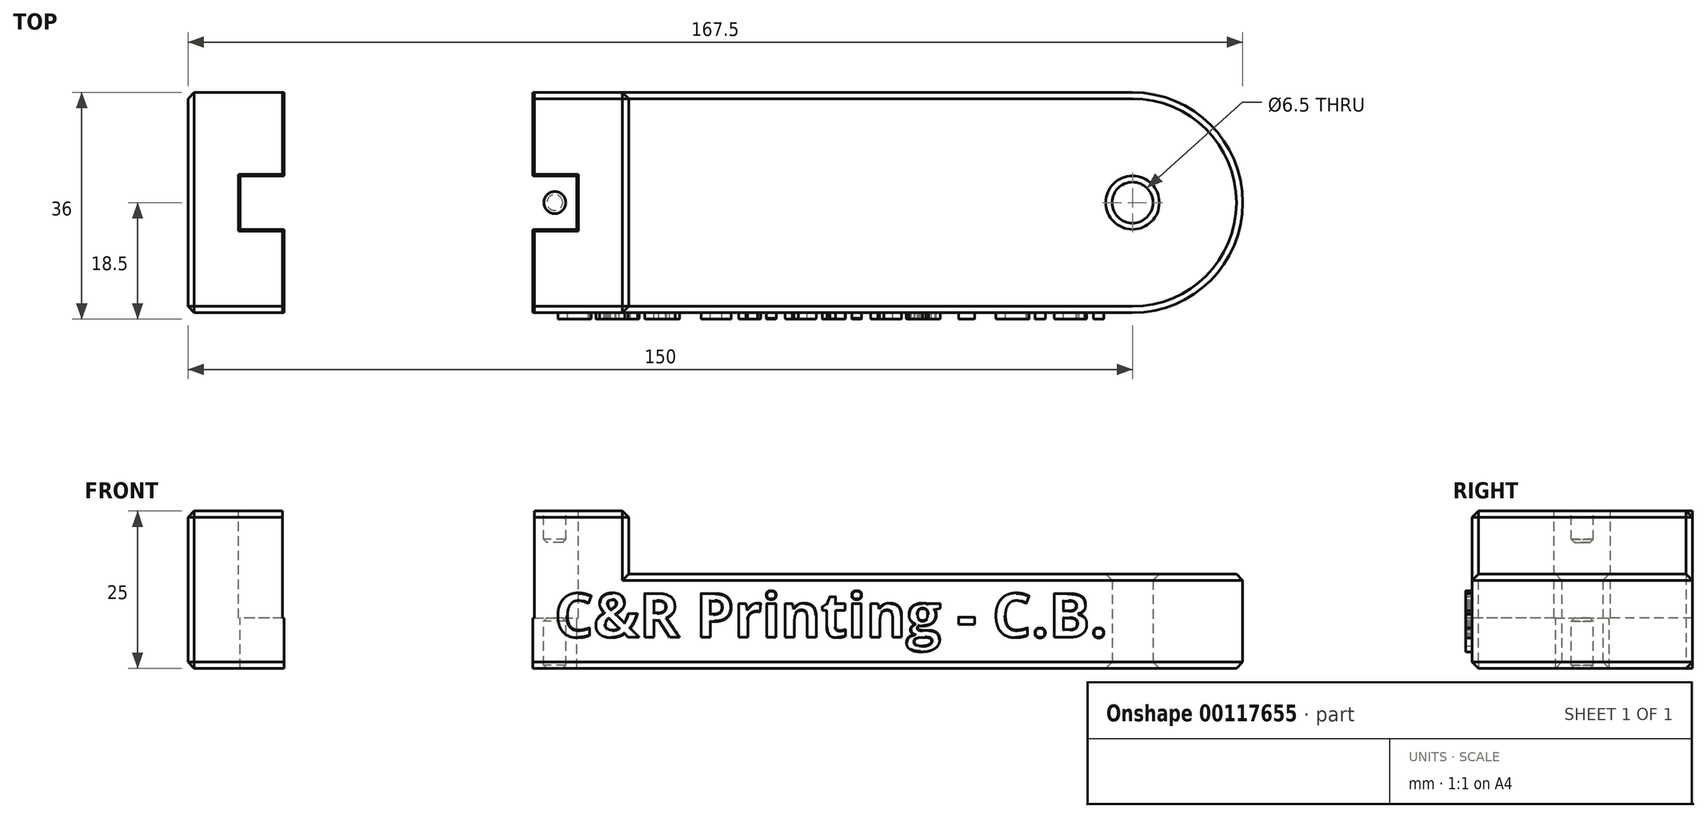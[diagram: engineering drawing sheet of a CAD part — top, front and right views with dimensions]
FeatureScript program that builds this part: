
annotation { "Feature Type Name" : "Feature", "Feature Type Description" : "" }
export const myFeature = defineFeature(function(context is Context, id is Id, definition is map)
    precondition{}
    {
        {
            var Q0;
            Q0=qCreatedBy(makeId("Top.planeOp"),FACE);
            var sketch = newSketch(context, id + "F0", { "sketchPlane" : qUnion([Q0])});
            skLineSegment(sketch, "E0.bottom", {"start": v(75, -17.5) * mm, "end": v(-75, -17.5) * mm});
            skLineSegment(sketch, "E0.top", {"start": v(75, 17.5) * mm, "end": v(-75, 17.5) * mm});
            skLineSegment(sketch, "E0.right", {"start": v(-75, -17.5) * mm, "end": v(-75, 17.5) * mm});
            skPoint(sketch, "E0.middle", {"position": v(0, 0) * mm});
            skPoint(sketch, "E1", {"position": v(75, 0) * mm});
            skArc(sketch, "E2", {"start": v(75, -17.5) * mm, "mid": v(92.5, 0) * mm, "end": v(75, 17.5) * mm});
            skCircle(sketch, "E3", {"center": v(75, 0) * mm, "radius": 3.25 * mm});
            skSolve(sketch);
        }
        {
            var Q0;
            Q0 = qSketchRegion(id + "F0", true);
            extrude(context, id + "F1", {"entities" : qUnion([Q0]), "depth" : 15 * mm});
        }
        {
            var Q0;
            Q0=makeQuery(id+"F1.opExtrude","CAP_FACE",FACE,{"disambiguationData":[OSD([sQuery(id+"F0.wireOp",EDGE,"E0.bottom"),sQuery(id+"F0.wireOp",EDGE,"E0.top"),sQuery(id+"F0.wireOp",EDGE,"E0.right"),sQuery(id+"F0.wireOp",EDGE,"E2"),sQuery(id+"F0.wireOp",EDGE,"E3")])],"isStart":false});
            var sketch = newSketch(context, id + "F2", { "sketchPlane" : qUnion([Q0])});
            skLineSegment(sketch, "E4.bottom", {"start": v(-75, 17.5) * mm, "end": v(-5, 17.5) * mm});
            skLineSegment(sketch, "E4.top", {"start": v(-75, -17.5) * mm, "end": v(-5, -17.5) * mm});
            skLineSegment(sketch, "E4.left", {"start": v(-75, 17.5) * mm, "end": v(-75, -17.5) * mm});
            skLineSegment(sketch, "E4.right", {"start": v(-5, 17.5) * mm, "end": v(-5, -17.5) * mm});
            skPoint(sketch, "E5", {"position": v(-60, 17.5) * mm});
            skLineSegment(sketch, "E6.bottom", {"start": v(-60, 17.5) * mm, "end": v(-20, 17.5) * mm});
            skLineSegment(sketch, "E6.top", {"start": v(-60, -17.5) * mm, "end": v(-20, -17.5) * mm});
            skLineSegment(sketch, "E6.right", {"start": v(-20, 17.5) * mm, "end": v(-20, -17.5) * mm});
            skLineSegment(sketch, "E7.bottom", {"start": v(-60, -4.5) * mm, "end": v(-67, -4.5) * mm});
            skLineSegment(sketch, "E7.top", {"start": v(-60, 4.5) * mm, "end": v(-67, 4.5) * mm});
            skLineSegment(sketch, "E7.right", {"start": v(-67, -4.5) * mm, "end": v(-67, 4.5) * mm});
            skPoint(sketch, "E8", {"position": v(-40, 17.5) * mm});
            skLineSegment(sketch, "E9", {"start": v(-40, 82.16) * mm, "end": v(-40, 3333.7) * mm, "construction": true});
            skLineSegment(sketch, "E10", {"start": v(-67, 4.5) * mm, "end": v(-67, 17.5) * mm});
            skLineSegment(sketch, "E11", {"start": v(-60, 17.5) * mm, "end": v(-67, 17.5) * mm});
            skLineSegment(sketch, "E12", {"start": v(-67, -4.5) * mm, "end": v(-67, -17.5) * mm});
            skLineSegment(sketch, "E13", {"start": v(-60, -17.5) * mm, "end": v(-67, -17.5) * mm});
            skLineSegment(sketch, "E14.MirrorCS", {"start": v(-13, 4.5) * mm, "end": v(-13, 17.5) * mm});
            skLineSegment(sketch, "E15.MirrorCS", {"start": v(-20, 4.5) * mm, "end": v(-13, 4.5) * mm});
            skLineSegment(sketch, "E16.MirrorCS", {"start": v(-20, -4.5) * mm, "end": v(-13, -4.5) * mm});
            skLineSegment(sketch, "E17.MirrorCS", {"start": v(-13, -4.5) * mm, "end": v(-13, 4.5) * mm});
            skLineSegment(sketch, "E18.MirrorCS", {"start": v(-13, -4.5) * mm, "end": v(-13, -17.5) * mm});
            skLineSegment(sketch, "E19.MirrorCS", {"start": v(-20, -17.5) * mm, "end": v(-13, -17.5) * mm});
            skLineSegment(sketch, "E20", {"start": v(-20, 17.5) * mm, "end": v(-13, 17.5) * mm});
            skLineSegment(sketch, "E21", {"start": v(-60, 17.5) * mm, "end": v(-60, -17.5) * mm});
            skPoint(sketch, "E22", {"position": v(-5, 0) * mm});
            skPoint(sketch, "E23", {"position": v(-40, -17.5) * mm});
            skPoint(sketch, "E24", {"position": v(-75, 0) * mm});
            skPoint(sketch, "E25", {"position": v(-40, 0) * mm});
            skSolve(sketch);
        }
        {
            var Q0;
            Q0 = qSketchRegion(id + "F2", true);
            var Q1;
            {var subQ0=sQuery(id+"F2.wireOp",EDGE,"E7.top");Q1=makeQuery(id+"F2.imprint","IMPRINT",FACE,{"disambiguationData":[TD([[makeQuery(id+"F2.imprint","IMPRINT",EDGE,{"derivedFrom":subQ0}),-1.0]])]});}
            var Q2;
            {var subQ0=sQuery(id+"F2.wireOp",EDGE,"E7.bottom");Q2=makeQuery(id+"F2.imprint","IMPRINT",FACE,{"disambiguationData":[TD([[makeQuery(id+"F2.imprint","IMPRINT",EDGE,{"derivedFrom":subQ0}),-1.0]])]});}
            var Q3;
            {var subQ0=sQuery(id+"F2.wireOp",EDGE,"E7.bottom");Q3=makeQuery(id+"F2.imprint","IMPRINT",FACE,{"disambiguationData":[TD([[makeQuery(id+"F2.imprint","IMPRINT",EDGE,{"derivedFrom":subQ0}),1.0]])]});}
            var Q4;
            {var subQ4=sQuery(id+"F2.wireOp",EDGE,"E6.bottom");Q4=makeQuery(id+"F2.imprint","IMPRINT",FACE,{"disambiguationData":[TD([[makeQuery(id+"F2.imprint","IMPRINT",EDGE,{"derivedFrom":subQ4}),-1.0]])]});}
            var Q5;
            {var subQ2=sQuery(id+"F2.wireOp",EDGE,"E16.MirrorCS");Q5=makeQuery(id+"F2.imprint","IMPRINT",FACE,{"disambiguationData":[TD([[makeQuery(id+"F2.imprint","IMPRINT",EDGE,{"derivedFrom":subQ2}),-1.0]])]});}
            var Q6;
            {var subQ0=sQuery(id+"F2.wireOp",EDGE,"E15.MirrorCS");Q6=makeQuery(id+"F2.imprint","IMPRINT",FACE,{"disambiguationData":[TD([[makeQuery(id+"F2.imprint","IMPRINT",EDGE,{"derivedFrom":subQ0}),-1.0]])]});}
            var Q7;
            Q7=makeQuery(id+"F2.imprint","IMPRINT",FACE,{"disambiguationData":[TD([[makeQuery(id+"F2.imprint","IMPRINT",EDGE,{"derivedFrom":sQuery(id+"F2.wireOp",EDGE,"E14.MirrorCS")}),1.0]])]});
            extrude(context, id + "F3", {"entities" : qUnion([Q0, Q1, Q2, Q3, Q4, Q5, Q6, Q7]), "operationType" : NewBodyOperationType.ADD, "depth" : 10 * mm});
        }
        {
            var Q0;
            Q0=makeQuery(id+"F3.opExtrude","CAP_FACE",FACE,{"disambiguationData":[OSD([sQuery(id+"F2.wireOp",EDGE,"E4.bottom"),sQuery(id+"F2.wireOp",EDGE,"E4.top"),sQuery(id+"F2.wireOp",EDGE,"E4.left"),sQuery(id+"F2.wireOp",EDGE,"E4.right")])],"isStart":false});
            cPlane(context, id + "F4", {"entities" : qUnion([Q0]), "cplaneType" : CPlaneType.OFFSET, "offset" : 0 * mm, "width" : 150 * mm, "height" : 150 * mm});
        }
        {
            var Q0;
            Q0=qCreatedBy(id+"F4.planeOp",FACE);
            var sketch = newSketch(context, id + "F5", { "sketchPlane" : qUnion([Q0])});
            skLineSegment(sketch, "E26.0", {"start": v(-20, 17.5) * mm, "end": v(-20, -17.5) * mm});
            skLineSegment(sketch, "E26.1", {"start": v(-60, 4.5) * mm, "end": v(-67, 4.5) * mm});
            skLineSegment(sketch, "E26.2", {"start": v(-67, -4.5) * mm, "end": v(-67, 4.5) * mm});
            skLineSegment(sketch, "E26.3", {"start": v(-13, -4.5) * mm, "end": v(-13, 4.5) * mm});
            skLineSegment(sketch, "E26.4", {"start": v(-67, 4.5) * mm, "end": v(-67, 17.5) * mm});
            skLineSegment(sketch, "E26.5", {"start": v(-60, 17.5) * mm, "end": v(-60, -17.5) * mm});
            skLineSegment(sketch, "E26.6", {"start": v(-13, 4.5) * mm, "end": v(-13, 17.5) * mm});
            skLineSegment(sketch, "E26.7", {"start": v(-60, -17.5) * mm, "end": v(-67, -17.5) * mm});
            skLineSegment(sketch, "E26.8", {"start": v(-60, -4.5) * mm, "end": v(-67, -4.5) * mm});
            skLineSegment(sketch, "E26.9", {"start": v(-20, -4.5) * mm, "end": v(-13, -4.5) * mm});
            skLineSegment(sketch, "E26.10", {"start": v(-20, 4.5) * mm, "end": v(-13, 4.5) * mm});
            skLineSegment(sketch, "E26.11", {"start": v(-20, -17.5) * mm, "end": v(-13, -17.5) * mm});
            skLineSegment(sketch, "E26.12", {"start": v(-60, 17.5) * mm, "end": v(-67, 17.5) * mm});
            skLineSegment(sketch, "E26.13", {"start": v(-67, -4.5) * mm, "end": v(-67, -17.5) * mm});
            skLineSegment(sketch, "E26.14", {"start": v(-60, -17.5) * mm, "end": v(-20, -17.5) * mm});
            skLineSegment(sketch, "E26.15", {"start": v(-60, 17.5) * mm, "end": v(-20, 17.5) * mm});
            skLineSegment(sketch, "E26.16", {"start": v(-20, 17.5) * mm, "end": v(-13, 17.5) * mm});
            skLineSegment(sketch, "E26.17", {"start": v(-13, -4.5) * mm, "end": v(-13, -17.5) * mm});
            skSolve(sketch);
        }
        {
            var Q0;
            {var subQ0=sQuery(id+"F5.wireOp",EDGE,"E26.1");Q0=makeQuery(id+"F5.imprint","IMPRINT",FACE,{"disambiguationData":[TD([[makeQuery(id+"F5.imprint","IMPRINT",EDGE,{"derivedFrom":subQ0}),1.0]])]});}
            var Q1;
            {var subQ6=sQuery(id+"F5.wireOp",EDGE,"E26.14");Q1=makeQuery(id+"F5.imprint","IMPRINT",FACE,{"disambiguationData":[TD([[makeQuery(id+"F5.imprint","IMPRINT",EDGE,{"derivedFrom":subQ6}),1.0]])]});}
            var Q2;
            Q2=makeQuery(id+"F5.imprint","IMPRINT",FACE,{"disambiguationData":[TD([[makeQuery(id+"F5.imprint","IMPRINT",EDGE,{"derivedFrom":sQuery(id+"F5.wireOp",EDGE,"E26.3")}),1.0]])]});
            extrude(context, id + "F6", {"entities" : qUnion([Q0, Q1, Q2]), "operationType" : NewBodyOperationType.REMOVE, "oppositeDirection" : true, "depth" : 17 * mm});
        }
        {
            var Q0;
            Q0 = qSketchRegion(id + "F5", true);
            extrude(context, id + "F7", {"entities" : qUnion([Q0]), "oppositeDirection" : true, "depth" : 5 * mm});
        }
        {
            var Q0;
            Q0=makeQuery(id+"F1.opExtrude","SWEPT_BODY",BODY,{"disambiguationData":[OSD([sQuery(id+"F0.wireOp",EDGE,"E0.bottom"),sQuery(id+"F0.wireOp",EDGE,"E0.top"),sQuery(id+"F0.wireOp",EDGE,"E0.right"),sQuery(id+"F0.wireOp",EDGE,"E2"),sQuery(id+"F0.wireOp",EDGE,"E3")])]});
            var Q1;
            Q1=makeQuery(id+"F7.opExtrude","SWEPT_BODY",BODY,{"disambiguationData":[OSD([sQuery(id+"F5.wireOp",EDGE,"E26.2"),sQuery(id+"F5.wireOp",EDGE,"E26.3"),sQuery(id+"F5.wireOp",EDGE,"E26.4"),sQuery(id+"F5.wireOp",EDGE,"E26.6"),sQuery(id+"F5.wireOp",EDGE,"E26.7"),sQuery(id+"F5.wireOp",EDGE,"E26.11"),sQuery(id+"F5.wireOp",EDGE,"E26.12"),sQuery(id+"F5.wireOp",EDGE,"E26.13"),sQuery(id+"F5.wireOp",EDGE,"E26.14"),sQuery(id+"F5.wireOp",EDGE,"E26.15"),sQuery(id+"F5.wireOp",EDGE,"E26.16"),sQuery(id+"F5.wireOp",EDGE,"E26.17")])]});
            var Q2;
            Q2=makeQuery(id+"F6.boolean.opBoolean","COPY",FACE,{"derivedFrom":makeQuery(id+"F6.opExtrude","SWEPT_FACE",FACE,{"disambiguationData":[OSD([sQuery(id+"F5.wireOp",EDGE,"E26.1")])]})});
            var Q3;
            Q3=makeQuery(id+"F6.boolean.opBoolean","COPY",FACE,{"derivedFrom":makeQuery(id+"F6.opExtrude","SWEPT_FACE",FACE,{"disambiguationData":[OSD([sQuery(id+"F5.wireOp",EDGE,"E26.2")])]})});
            var Q4;
            Q4=makeQuery(id+"F6.boolean.opBoolean","COPY",FACE,{"derivedFrom":makeQuery(id+"F6.opExtrude","SWEPT_FACE",FACE,{"disambiguationData":[OSD([sQuery(id+"F5.wireOp",EDGE,"E26.8")])]})});
            var Q5;
            {var subQ0=sQuery(id+"F5.wireOp",EDGE,"E26.5");Q5=makeQuery(id+"F6.boolean.opBoolean","COPY",FACE,{"derivedFrom":makeQuery(id+"F6.opExtrude","SWEPT_FACE",FACE,{"disambiguationData":[OSD([subQ0]),TDD([makeQuery(id+"F5.imprint","IMPRINT",EDGE,{"disambiguationData":[TD([[makeQuery(id+"F5.imprint","INTERSECT",VERTEX,{"derivedFrom":[subQ0,sQuery(id+"F5.wireOp",EDGE,"E26.8")]}),-1.0]])],"derivedFrom":subQ0})])]})});}
            var Q6;
            {var subQ0=sQuery(id+"F5.wireOp",EDGE,"E26.5");Q6=makeQuery(id+"F6.boolean.opBoolean","COPY",FACE,{"derivedFrom":makeQuery(id+"F6.opExtrude","SWEPT_FACE",FACE,{"disambiguationData":[OSD([subQ0]),TDD([makeQuery(id+"F5.imprint","IMPRINT",EDGE,{"disambiguationData":[TD([[makeQuery(id+"F5.imprint","INTERSECT",VERTEX,{"derivedFrom":[sQuery(id+"F5.wireOp",EDGE,"E26.1"),subQ0]}),1.0]])],"derivedFrom":subQ0})])]})});}
            var Q7;
            {var subQ0=sQuery(id+"F5.wireOp",EDGE,"E26.0");Q7=makeQuery(id+"F6.boolean.opBoolean","COPY",FACE,{"derivedFrom":makeQuery(id+"F6.opExtrude","SWEPT_FACE",FACE,{"disambiguationData":[OSD([subQ0]),TDD([makeQuery(id+"F5.imprint","IMPRINT",EDGE,{"disambiguationData":[TD([[makeQuery(id+"F5.imprint","INTERSECT",VERTEX,{"derivedFrom":[subQ0,sQuery(id+"F5.wireOp",EDGE,"E26.9")]}),-1.0]])],"derivedFrom":subQ0})])]})});}
            var Q8;
            Q8=makeQuery(id+"F6.boolean.opBoolean","COPY",FACE,{"derivedFrom":makeQuery(id+"F6.opExtrude","SWEPT_FACE",FACE,{"disambiguationData":[OSD([sQuery(id+"F5.wireOp",EDGE,"E26.3")])]})});
            var Q9;
            {var subQ0=sQuery(id+"F5.wireOp",EDGE,"E26.0");Q9=makeQuery(id+"F6.boolean.opBoolean","COPY",FACE,{"derivedFrom":makeQuery(id+"F6.opExtrude","SWEPT_FACE",FACE,{"disambiguationData":[OSD([subQ0]),TDD([makeQuery(id+"F5.imprint","IMPRINT",EDGE,{"disambiguationData":[TD([[makeQuery(id+"F5.imprint","INTERSECT",VERTEX,{"derivedFrom":[subQ0,sQuery(id+"F5.wireOp",EDGE,"E26.10")]}),1.0]])],"derivedFrom":subQ0})])]})});}
            var Q10;
            Q10=makeQuery(id+"F6.boolean.opBoolean","COPY",FACE,{"derivedFrom":makeQuery(id+"F6.opExtrude","SWEPT_FACE",FACE,{"disambiguationData":[OSD([sQuery(id+"F5.wireOp",EDGE,"E26.10")])]})});
            var Q11;
            Q11=makeQuery(id+"F6.boolean.opBoolean","COPY",FACE,{"derivedFrom":makeQuery(id+"F6.opExtrude","SWEPT_FACE",FACE,{"disambiguationData":[OSD([sQuery(id+"F5.wireOp",EDGE,"E26.9")])]})});
            booleanBodies(context, id + "F8", {"operationType" : BooleanOperationType.SUBTRACTION, "tools" : qUnion([Q0]), "targets" : qUnion([Q1]), "offset" : true, "entitiesToOffset" : qUnion([Q2, Q3, Q4, Q5, Q6, Q7, Q8, Q9, Q10, Q11]), "offsetDistance" : .25 * mm, "keepTools" : true});
        }
        {
            var Q0;
            Q0=makeQuery(id+"F7.opExtrude","CAP_FACE",FACE,{"disambiguationData":[OSD([sQuery(id+"F5.wireOp",EDGE,"E26.2"),sQuery(id+"F5.wireOp",EDGE,"E26.3"),sQuery(id+"F5.wireOp",EDGE,"E26.4"),sQuery(id+"F5.wireOp",EDGE,"E26.6"),sQuery(id+"F5.wireOp",EDGE,"E26.7"),sQuery(id+"F5.wireOp",EDGE,"E26.11"),sQuery(id+"F5.wireOp",EDGE,"E26.12"),sQuery(id+"F5.wireOp",EDGE,"E26.13"),sQuery(id+"F5.wireOp",EDGE,"E26.14"),sQuery(id+"F5.wireOp",EDGE,"E26.15"),sQuery(id+"F5.wireOp",EDGE,"E26.16"),sQuery(id+"F5.wireOp",EDGE,"E26.17")])],"isStart":true});
            var sketch = newSketch(context, id + "F9", { "sketchPlane" : qUnion([Q0])});
            skPoint(sketch, "E27", {"position": v(-66.75, 4.25) * mm});
            skPoint(sketch, "E28", {"position": v(-59.75, 4.25) * mm});
            skPoint(sketch, "E29", {"position": v(-63.25, 4.25) * mm});
            skPoint(sketch, "E30", {"position": v(-66.75, 0) * mm});
            skPoint(sketch, "E31", {"position": v(-63.25, 0) * mm});
            skLineSegment(sketch, "E32", {"start": v(-40, 25.57) * mm, "end": v(-40, -23.42) * mm, "construction": true});
            skPoint(sketch, "E32.startSnap0", {"position": v(-40, 17.5) * mm});
            skPoint(sketch, "E33.MirrorP", {"position": v(-16.75, 0) * mm});
            skCircle(sketch, "E34", {"center": v(-63.25, 0) * mm, "radius": 1.75 * mm});
            skCircle(sketch, "E35.MirrorC", {"center": v(-16.75, 0) * mm, "radius": 1.75 * mm});
            skSolve(sketch);
        }
        {
            var Q0;
            Q0=makeQuery(id+"F9.imprint","IMPRINT",FACE,{"disambiguationData":[TD([[makeQuery(id+"F9.imprint","IMPRINT",EDGE,{"derivedFrom":sQuery(id+"F9.wireOp",EDGE,"E34")}),1.0]])]});
            var Q1;
            Q1=makeQuery(id+"F9.imprint","IMPRINT",FACE,{"disambiguationData":[TD([[makeQuery(id+"F9.imprint","IMPRINT",EDGE,{"derivedFrom":sQuery(id+"F9.wireOp",EDGE,"E35.MirrorC")}),-1.0]])]});
            extrude(context, id + "F10", {"entities" : qUnion([Q0, Q1]), "operationType" : NewBodyOperationType.REMOVE, "endBound" : BoundingType.THROUGH_ALL, "oppositeDirection" : true, "depth" : 25 * mm});
        }
        {
            var Q0;
            Q0=makeQuery(id+"F1.opExtrude","CAP_EDGE",EDGE,{"disambiguationData":[OSD([sQuery(id+"F0.wireOp",EDGE,"E3")])],"isStart":true});
            var Q1;
            Q1=makeQuery(id+"F1.opExtrude","CAP_EDGE",EDGE,{"disambiguationData":[OSD([sQuery(id+"F0.wireOp",EDGE,"E3")])],"isStart":false});
            var Q2;
            Q2=makeQuery(id+"F1.opExtrude","CAP_EDGE",EDGE,{"disambiguationData":[OSD([sQuery(id+"F0.wireOp",EDGE,"E0.bottom")])],"isStart":false});
            var Q3;
            Q3=makeQuery(id+"F1.opExtrude","CAP_EDGE",EDGE,{"disambiguationData":[OSD([sQuery(id+"F0.wireOp",EDGE,"E0.bottom")])],"isStart":true});
            var Q4;
            Q4=makeQuery(id+"F1.opExtrude","CAP_EDGE",EDGE,{"disambiguationData":[OSD([sQuery(id+"F0.wireOp",EDGE,"E0.right")])],"isStart":true});
            var Q5;
            Q5=makeQuery(id+"F3.opExtrude","CAP_EDGE",EDGE,{"disambiguationData":[OSD([sQuery(id+"F2.wireOp",EDGE,"E4.left")])],"isStart":false});
            var Q6;
            {var subQ0=sQuery(id+"F2.wireOp",EDGE,"E19.MirrorCS");var subQ1=sQuery(id+"F2.wireOp",EDGE,"E13");var subQ2=sQuery(id+"F2.wireOp",EDGE,"E6.top");var subQ4=sQuery(id+"F2.wireOp",EDGE,"E4.top");Q6=makeQuery(id+"F6.boolean.opBoolean","SPLIT",EDGE,{"disambiguationData":[TD([makeQuery(id+"F1.opExtrude","SWEPT_FACE",FACE,{"disambiguationData":[OSD([sQuery(id+"F0.wireOp",EDGE,"E0.right")])]})])],"derivedFrom":makeQuery(id+"F3.opExtrude","CAP_EDGE",EDGE,{"disambiguationData":[OSD([subQ4,subQ2,subQ1,subQ0])],"isStart":false})});}
            var Q7;
            {var subQ0=sQuery(id+"F2.wireOp",EDGE,"E4.right");var subQ1=sQuery(id+"F2.wireOp",EDGE,"E19.MirrorCS");var subQ2=sQuery(id+"F2.wireOp",EDGE,"E13");var subQ3=sQuery(id+"F2.wireOp",EDGE,"E6.top");var subQ4=sQuery(id+"F2.wireOp",EDGE,"E4.top");Q7=makeQuery(id+"F6.boolean.opBoolean","SPLIT",EDGE,{"disambiguationData":[TD([makeQuery(id+"F3.opExtrude","SWEPT_FACE",FACE,{"disambiguationData":[OSD([subQ0])]})])],"derivedFrom":makeQuery(id+"F3.opExtrude","CAP_EDGE",EDGE,{"disambiguationData":[OSD([subQ4,subQ3,subQ2,subQ1])],"isStart":false})});}
            var Q8;
            Q8=makeQuery(id+"F3.opExtrude","CAP_EDGE",EDGE,{"disambiguationData":[OSD([sQuery(id+"F2.wireOp",EDGE,"E4.right")])],"isStart":false});
            var Q9;
            {var subQ0=sQuery(id+"F2.wireOp",EDGE,"E4.right");var subQ1=sQuery(id+"F2.wireOp",EDGE,"E20");var subQ2=sQuery(id+"F2.wireOp",EDGE,"E11");var subQ3=sQuery(id+"F2.wireOp",EDGE,"E6.bottom");var subQ4=sQuery(id+"F2.wireOp",EDGE,"E4.bottom");Q9=makeQuery(id+"F6.boolean.opBoolean","SPLIT",EDGE,{"disambiguationData":[TD([makeQuery(id+"F3.opExtrude","SWEPT_FACE",FACE,{"disambiguationData":[OSD([subQ0])]})])],"derivedFrom":makeQuery(id+"F3.opExtrude","CAP_EDGE",EDGE,{"disambiguationData":[OSD([subQ4,subQ3,subQ2,subQ1])],"isStart":false})});}
            var Q10;
            Q10=makeQuery(id+"F3.opExtrude","SWEPT_EDGE",EDGE,{"disambiguationData":[OSD([sQuery(id+"F0.wireOp",EDGE,"E0.top"),sQuery(id+"F2.wireOp",EDGE,"E4.bottom"),sQuery(id+"F2.wireOp",EDGE,"E4.right")])]});
            var Q11;
            Q11=makeQuery(id+"F3.opExtrude","SWEPT_EDGE",EDGE,{"disambiguationData":[OSD([sQuery(id+"F0.wireOp",EDGE,"E0.bottom"),sQuery(id+"F2.wireOp",EDGE,"E4.top"),sQuery(id+"F2.wireOp",EDGE,"E4.right")])]});
            var Q12;
            Q12=makeQuery(id+"F3.boolean.opBoolean","MERGE",EDGE,{"derivedFrom":[makeQuery(id+"F1.opExtrude","SWEPT_EDGE",EDGE,{"disambiguationData":[OSD([sQuery(id+"F0.wireOp",EDGE,"E0.top"),sQuery(id+"F0.wireOp",EDGE,"E0.right")])]}),makeQuery(id+"F3.opExtrude","SWEPT_EDGE",EDGE,{"disambiguationData":[OSD([sQuery(id+"F2.wireOp",EDGE,"E4.bottom"),sQuery(id+"F2.wireOp",EDGE,"E4.left")])]})]});
            var Q13;
            Q13=makeQuery(id+"F3.boolean.opBoolean","MERGE",EDGE,{"derivedFrom":[makeQuery(id+"F1.opExtrude","SWEPT_EDGE",EDGE,{"disambiguationData":[OSD([sQuery(id+"F0.wireOp",EDGE,"E0.bottom"),sQuery(id+"F0.wireOp",EDGE,"E0.right")])]}),makeQuery(id+"F3.opExtrude","SWEPT_EDGE",EDGE,{"disambiguationData":[OSD([sQuery(id+"F2.wireOp",EDGE,"E4.top"),sQuery(id+"F2.wireOp",EDGE,"E4.left")])]})]});
            chamfer(context, id + "F11", {"entities" : qUnion([Q0, Q1, Q2, Q3, Q4, Q5, Q6, Q7, Q8, Q9, Q10, Q11, Q12, Q13]), "width" : 1 * mm, "tangentPropagation" : true});
        }
        {
            var Q0;
            Q0=makeQuery(id+"F10.boolean.opBoolean","INTERSECT",EDGE,{"derivedFrom":[makeQuery(id+"F6.boolean.opBoolean","COPY",FACE,{"derivedFrom":makeQuery(id+"F6.opExtrude","CAP_FACE",FACE,{"disambiguationData":[OSD([sQuery(id+"F5.wireOp",EDGE,"E26.0"),sQuery(id+"F5.wireOp",EDGE,"E26.1"),sQuery(id+"F5.wireOp",EDGE,"E26.2"),sQuery(id+"F5.wireOp",EDGE,"E26.3"),sQuery(id+"F5.wireOp",EDGE,"E26.5"),sQuery(id+"F5.wireOp",EDGE,"E26.8"),sQuery(id+"F5.wireOp",EDGE,"E26.9"),sQuery(id+"F5.wireOp",EDGE,"E26.10"),sQuery(id+"F5.wireOp",EDGE,"E26.14"),sQuery(id+"F5.wireOp",EDGE,"E26.15")])],"isStart":false})}),makeQuery(id+"F10.opExtrude","SWEPT_FACE",FACE,{"disambiguationData":[OSD([sQuery(id+"F9.wireOp",EDGE,"E34")])]})]});
            var Q1;
            Q1=makeQuery(id+"F10.boolean.opBoolean","INTERSECT",EDGE,{"derivedFrom":[makeQuery(id+"F1.opExtrude","CAP_FACE",FACE,{"disambiguationData":[OSD([sQuery(id+"F0.wireOp",EDGE,"E0.bottom"),sQuery(id+"F0.wireOp",EDGE,"E0.top"),sQuery(id+"F0.wireOp",EDGE,"E0.right"),sQuery(id+"F0.wireOp",EDGE,"E2"),sQuery(id+"F0.wireOp",EDGE,"E3")])],"isStart":true}),makeQuery(id+"F10.opExtrude","SWEPT_FACE",FACE,{"disambiguationData":[OSD([sQuery(id+"F9.wireOp",EDGE,"E34")])]})]});
            var Q2;
            Q2=makeQuery(id+"F10.boolean.opBoolean","INTERSECT",EDGE,{"derivedFrom":[makeQuery(id+"F1.opExtrude","CAP_FACE",FACE,{"disambiguationData":[OSD([sQuery(id+"F0.wireOp",EDGE,"E0.bottom"),sQuery(id+"F0.wireOp",EDGE,"E0.top"),sQuery(id+"F0.wireOp",EDGE,"E0.right"),sQuery(id+"F0.wireOp",EDGE,"E2"),sQuery(id+"F0.wireOp",EDGE,"E3")])],"isStart":true}),makeQuery(id+"F10.opExtrude","SWEPT_FACE",FACE,{"disambiguationData":[OSD([sQuery(id+"F9.wireOp",EDGE,"E35.MirrorC")])]})]});
            var Q3;
            Q3=makeQuery(id+"F10.boolean.opBoolean","INTERSECT",EDGE,{"derivedFrom":[makeQuery(id+"F6.boolean.opBoolean","COPY",FACE,{"derivedFrom":makeQuery(id+"F6.opExtrude","CAP_FACE",FACE,{"disambiguationData":[OSD([sQuery(id+"F5.wireOp",EDGE,"E26.0"),sQuery(id+"F5.wireOp",EDGE,"E26.1"),sQuery(id+"F5.wireOp",EDGE,"E26.2"),sQuery(id+"F5.wireOp",EDGE,"E26.3"),sQuery(id+"F5.wireOp",EDGE,"E26.5"),sQuery(id+"F5.wireOp",EDGE,"E26.8"),sQuery(id+"F5.wireOp",EDGE,"E26.9"),sQuery(id+"F5.wireOp",EDGE,"E26.10"),sQuery(id+"F5.wireOp",EDGE,"E26.14"),sQuery(id+"F5.wireOp",EDGE,"E26.15")])],"isStart":false})}),makeQuery(id+"F10.opExtrude","SWEPT_FACE",FACE,{"disambiguationData":[OSD([sQuery(id+"F9.wireOp",EDGE,"E35.MirrorC")])]})]});
            var Q4;
            Q4=makeQuery(id+"F10.boolean.opBoolean","COPY",EDGE,{"derivedFrom":makeQuery(id+"F10.opExtrude","CAP_EDGE",EDGE,{"disambiguationData":[OSD([sQuery(id+"F9.wireOp",EDGE,"E35.MirrorC")])],"isStart":true})});
            var Q5;
            Q5=makeQuery(id+"F10.boolean.opBoolean","COPY",EDGE,{"derivedFrom":makeQuery(id+"F10.opExtrude","CAP_EDGE",EDGE,{"disambiguationData":[OSD([sQuery(id+"F9.wireOp",EDGE,"E34")])],"isStart":true})});
            var Q6;
            Q6=makeQuery(id+"F10.boolean.opBoolean","INTERSECT",EDGE,{"derivedFrom":[makeQuery(id+"F7.opExtrude","CAP_FACE",FACE,{"disambiguationData":[OSD([sQuery(id+"F5.wireOp",EDGE,"E26.2"),sQuery(id+"F5.wireOp",EDGE,"E26.3"),sQuery(id+"F5.wireOp",EDGE,"E26.4"),sQuery(id+"F5.wireOp",EDGE,"E26.6"),sQuery(id+"F5.wireOp",EDGE,"E26.7"),sQuery(id+"F5.wireOp",EDGE,"E26.11"),sQuery(id+"F5.wireOp",EDGE,"E26.12"),sQuery(id+"F5.wireOp",EDGE,"E26.13"),sQuery(id+"F5.wireOp",EDGE,"E26.14"),sQuery(id+"F5.wireOp",EDGE,"E26.15"),sQuery(id+"F5.wireOp",EDGE,"E26.16"),sQuery(id+"F5.wireOp",EDGE,"E26.17")])],"isStart":false}),makeQuery(id+"F10.opExtrude","SWEPT_FACE",FACE,{"disambiguationData":[OSD([sQuery(id+"F9.wireOp",EDGE,"E35.MirrorC")])]})]});
            var Q7;
            Q7=makeQuery(id+"F10.boolean.opBoolean","INTERSECT",EDGE,{"derivedFrom":[makeQuery(id+"F7.opExtrude","CAP_FACE",FACE,{"disambiguationData":[OSD([sQuery(id+"F5.wireOp",EDGE,"E26.2"),sQuery(id+"F5.wireOp",EDGE,"E26.3"),sQuery(id+"F5.wireOp",EDGE,"E26.4"),sQuery(id+"F5.wireOp",EDGE,"E26.6"),sQuery(id+"F5.wireOp",EDGE,"E26.7"),sQuery(id+"F5.wireOp",EDGE,"E26.11"),sQuery(id+"F5.wireOp",EDGE,"E26.12"),sQuery(id+"F5.wireOp",EDGE,"E26.13"),sQuery(id+"F5.wireOp",EDGE,"E26.14"),sQuery(id+"F5.wireOp",EDGE,"E26.15"),sQuery(id+"F5.wireOp",EDGE,"E26.16"),sQuery(id+"F5.wireOp",EDGE,"E26.17")])],"isStart":false}),makeQuery(id+"F10.opExtrude","SWEPT_FACE",FACE,{"disambiguationData":[OSD([sQuery(id+"F9.wireOp",EDGE,"E34")])]})]});
            chamfer(context, id + "F12", {"entities" : qUnion([Q0, Q1, Q2, Q3, Q4, Q5, Q6, Q7]), "width" : .5 * mm, "tangentPropagation" : true});
        }
        {
            var Q0;
            Q0=makeQuery(id+"F3.boolean.opBoolean","MERGE",FACE,{"derivedFrom":[makeQuery(id+"F1.opExtrude","SWEPT_FACE",FACE,{"disambiguationData":[OSD([sQuery(id+"F0.wireOp",EDGE,"E0.bottom")])]}),makeQuery(id+"F3.opExtrude","SWEPT_FACE",FACE,{"disambiguationData":[OSD([sQuery(id+"F2.wireOp",EDGE,"E4.top"),sQuery(id+"F2.wireOp",EDGE,"E6.top"),sQuery(id+"F2.wireOp",EDGE,"E13"),sQuery(id+"F2.wireOp",EDGE,"E19.MirrorCS")])]})]});
            var sketch = newSketch(context, id + "F13", { "sketchPlane" : qUnion([Q0])});
            skText(sketch, "E36", { "text": "C&R Printing - C.B.", "fontName": "OpenSans-Bold.ttf"});
            const initialGuessF13  = {"E36": [-0.01682, 0.00496, 1, 0, 0.007]};
            skSetInitialGuess(sketch, initialGuessF13);
            skSolve(sketch);
        }
        {
            var Q0;
            Q0 = qSketchRegion(id + "F13", true);
            extrude(context, id + "F14", {"entities" : qUnion([Q0]), "operationType" : NewBodyOperationType.ADD, "depth" : 1 * mm});
        }
        {
            var Q0;
            Q0=makeQuery(id+"F14.opExtrude","CAP_FACE",FACE,{"disambiguationData":[OSD([sQuery(id+"F13.wireOp",EDGE,"E36.sketch_text.stroke-0"),sQuery(id+"F13.wireOp",EDGE,"E36.sketch_text.stroke-1"),sQuery(id+"F13.wireOp",EDGE,"E36.sketch_text.stroke-2"),sQuery(id+"F13.wireOp",EDGE,"E36.sketch_text.stroke-3"),sQuery(id+"F13.wireOp",EDGE,"E36.sketch_text.stroke-4"),sQuery(id+"F13.wireOp",EDGE,"E36.sketch_text.stroke-5"),sQuery(id+"F13.wireOp",EDGE,"E36.sketch_text.stroke-6"),sQuery(id+"F13.wireOp",EDGE,"E36.sketch_text.stroke-7"),sQuery(id+"F13.wireOp",EDGE,"E36.sketch_text.stroke-8"),sQuery(id+"F13.wireOp",EDGE,"E36.sketch_text.stroke-9"),sQuery(id+"F13.wireOp",EDGE,"E36.sketch_text.stroke-10"),sQuery(id+"F13.wireOp",EDGE,"E36.sketch_text.stroke-11"),sQuery(id+"F13.wireOp",EDGE,"E36.sketch_text.stroke-12"),sQuery(id+"F13.wireOp",EDGE,"E36.sketch_text.stroke-13"),sQuery(id+"F13.wireOp",EDGE,"E36.sketch_text.stroke-14")])],"isStart":false});
            var Q1;
            Q1=makeQuery(id+"F14.opExtrude","CAP_FACE",FACE,{"disambiguationData":[OSD([sQuery(id+"F13.wireOp",EDGE,"E36.sketch_text.stroke-15"),sQuery(id+"F13.wireOp",EDGE,"E36.sketch_text.stroke-16"),sQuery(id+"F13.wireOp",EDGE,"E36.sketch_text.stroke-17"),sQuery(id+"F13.wireOp",EDGE,"E36.sketch_text.stroke-18"),sQuery(id+"F13.wireOp",EDGE,"E36.sketch_text.stroke-19"),sQuery(id+"F13.wireOp",EDGE,"E36.sketch_text.stroke-20"),sQuery(id+"F13.wireOp",EDGE,"E36.sketch_text.stroke-21"),sQuery(id+"F13.wireOp",EDGE,"E36.sketch_text.stroke-22"),sQuery(id+"F13.wireOp",EDGE,"E36.sketch_text.stroke-23"),sQuery(id+"F13.wireOp",EDGE,"E36.sketch_text.stroke-24"),sQuery(id+"F13.wireOp",EDGE,"E36.sketch_text.stroke-25"),sQuery(id+"F13.wireOp",EDGE,"E36.sketch_text.stroke-26"),sQuery(id+"F13.wireOp",EDGE,"E36.sketch_text.stroke-27"),sQuery(id+"F13.wireOp",EDGE,"E36.sketch_text.stroke-28"),sQuery(id+"F13.wireOp",EDGE,"E36.sketch_text.stroke-29"),sQuery(id+"F13.wireOp",EDGE,"E36.sketch_text.stroke-30"),sQuery(id+"F13.wireOp",EDGE,"E36.sketch_text.stroke-31"),sQuery(id+"F13.wireOp",EDGE,"E36.sketch_text.stroke-32"),sQuery(id+"F13.wireOp",EDGE,"E36.sketch_text.stroke-33"),sQuery(id+"F13.wireOp",EDGE,"E36.sketch_text.stroke-34"),sQuery(id+"F13.wireOp",EDGE,"E36.sketch_text.stroke-35"),sQuery(id+"F13.wireOp",EDGE,"E36.sketch_text.stroke-36"),sQuery(id+"F13.wireOp",EDGE,"E36.sketch_text.stroke-37"),sQuery(id+"F13.wireOp",EDGE,"E36.sketch_text.stroke-38"),sQuery(id+"F13.wireOp",EDGE,"E36.sketch_text.stroke-39"),sQuery(id+"F13.wireOp",EDGE,"E36.sketch_text.stroke-40"),sQuery(id+"F13.wireOp",EDGE,"E36.sketch_text.stroke-41"),sQuery(id+"F13.wireOp",EDGE,"E36.sketch_text.stroke-42"),sQuery(id+"F13.wireOp",EDGE,"E36.sketch_text.stroke-43"),sQuery(id+"F13.wireOp",EDGE,"E36.sketch_text.stroke-44"),sQuery(id+"F13.wireOp",EDGE,"E36.sketch_text.stroke-45"),sQuery(id+"F13.wireOp",EDGE,"E36.sketch_text.stroke-46"),sQuery(id+"F13.wireOp",EDGE,"E36.sketch_text.stroke-47"),sQuery(id+"F13.wireOp",EDGE,"E36.sketch_text.stroke-48")])],"isStart":false});
            var Q2;
            Q2=makeQuery(id+"F14.opExtrude","CAP_FACE",FACE,{"disambiguationData":[OSD([sQuery(id+"F13.wireOp",EDGE,"E36.sketch_text.stroke-49"),sQuery(id+"F13.wireOp",EDGE,"E36.sketch_text.stroke-50"),sQuery(id+"F13.wireOp",EDGE,"E36.sketch_text.stroke-51"),sQuery(id+"F13.wireOp",EDGE,"E36.sketch_text.stroke-52"),sQuery(id+"F13.wireOp",EDGE,"E36.sketch_text.stroke-53"),sQuery(id+"F13.wireOp",EDGE,"E36.sketch_text.stroke-54"),sQuery(id+"F13.wireOp",EDGE,"E36.sketch_text.stroke-55"),sQuery(id+"F13.wireOp",EDGE,"E36.sketch_text.stroke-56"),sQuery(id+"F13.wireOp",EDGE,"E36.sketch_text.stroke-57"),sQuery(id+"F13.wireOp",EDGE,"E36.sketch_text.stroke-58"),sQuery(id+"F13.wireOp",EDGE,"E36.sketch_text.stroke-59"),sQuery(id+"F13.wireOp",EDGE,"E36.sketch_text.stroke-60"),sQuery(id+"F13.wireOp",EDGE,"E36.sketch_text.stroke-61"),sQuery(id+"F13.wireOp",EDGE,"E36.sketch_text.stroke-62"),sQuery(id+"F13.wireOp",EDGE,"E36.sketch_text.stroke-63"),sQuery(id+"F13.wireOp",EDGE,"E36.sketch_text.stroke-64"),sQuery(id+"F13.wireOp",EDGE,"E36.sketch_text.stroke-65"),sQuery(id+"F13.wireOp",EDGE,"E36.sketch_text.stroke-66"),sQuery(id+"F13.wireOp",EDGE,"E36.sketch_text.stroke-67")])],"isStart":false});
            var Q3;
            Q3=makeQuery(id+"F14.opExtrude","CAP_FACE",FACE,{"disambiguationData":[OSD([sQuery(id+"F13.wireOp",EDGE,"E36.sketch_text.stroke-68"),sQuery(id+"F13.wireOp",EDGE,"E36.sketch_text.stroke-69"),sQuery(id+"F13.wireOp",EDGE,"E36.sketch_text.stroke-70"),sQuery(id+"F13.wireOp",EDGE,"E36.sketch_text.stroke-71"),sQuery(id+"F13.wireOp",EDGE,"E36.sketch_text.stroke-72"),sQuery(id+"F13.wireOp",EDGE,"E36.sketch_text.stroke-73"),sQuery(id+"F13.wireOp",EDGE,"E36.sketch_text.stroke-74"),sQuery(id+"F13.wireOp",EDGE,"E36.sketch_text.stroke-75"),sQuery(id+"F13.wireOp",EDGE,"E36.sketch_text.stroke-76"),sQuery(id+"F13.wireOp",EDGE,"E36.sketch_text.stroke-77"),sQuery(id+"F13.wireOp",EDGE,"E36.sketch_text.stroke-78"),sQuery(id+"F13.wireOp",EDGE,"E36.sketch_text.stroke-79"),sQuery(id+"F13.wireOp",EDGE,"E36.sketch_text.stroke-80"),sQuery(id+"F13.wireOp",EDGE,"E36.sketch_text.stroke-81"),sQuery(id+"F13.wireOp",EDGE,"E36.sketch_text.stroke-82"),sQuery(id+"F13.wireOp",EDGE,"E36.sketch_text.stroke-83")])],"isStart":false});
            var Q4;
            Q4=makeQuery(id+"F14.opExtrude","CAP_FACE",FACE,{"disambiguationData":[OSD([sQuery(id+"F13.wireOp",EDGE,"E36.sketch_text.stroke-84"),sQuery(id+"F13.wireOp",EDGE,"E36.sketch_text.stroke-85"),sQuery(id+"F13.wireOp",EDGE,"E36.sketch_text.stroke-86"),sQuery(id+"F13.wireOp",EDGE,"E36.sketch_text.stroke-87"),sQuery(id+"F13.wireOp",EDGE,"E36.sketch_text.stroke-88"),sQuery(id+"F13.wireOp",EDGE,"E36.sketch_text.stroke-89"),sQuery(id+"F13.wireOp",EDGE,"E36.sketch_text.stroke-90"),sQuery(id+"F13.wireOp",EDGE,"E36.sketch_text.stroke-91"),sQuery(id+"F13.wireOp",EDGE,"E36.sketch_text.stroke-92"),sQuery(id+"F13.wireOp",EDGE,"E36.sketch_text.stroke-93"),sQuery(id+"F13.wireOp",EDGE,"E36.sketch_text.stroke-94"),sQuery(id+"F13.wireOp",EDGE,"E36.sketch_text.stroke-95"),sQuery(id+"F13.wireOp",EDGE,"E36.sketch_text.stroke-96")])],"isStart":false});
            var Q5;
            Q5=makeQuery(id+"F14.opExtrude","CAP_FACE",FACE,{"disambiguationData":[OSD([sQuery(id+"F13.wireOp",EDGE,"E36.sketch_text.stroke-102"),sQuery(id+"F13.wireOp",EDGE,"E36.sketch_text.stroke-103"),sQuery(id+"F13.wireOp",EDGE,"E36.sketch_text.stroke-104"),sQuery(id+"F13.wireOp",EDGE,"E36.sketch_text.stroke-105")])],"isStart":false});
            var Q6;
            Q6=makeQuery(id+"F14.opExtrude","CAP_FACE",FACE,{"disambiguationData":[OSD([sQuery(id+"F13.wireOp",EDGE,"E36.sketch_text.stroke-97"),sQuery(id+"F13.wireOp",EDGE,"E36.sketch_text.stroke-98"),sQuery(id+"F13.wireOp",EDGE,"E36.sketch_text.stroke-99"),sQuery(id+"F13.wireOp",EDGE,"E36.sketch_text.stroke-100"),sQuery(id+"F13.wireOp",EDGE,"E36.sketch_text.stroke-101")])],"isStart":false});
            var Q7;
            Q7=makeQuery(id+"F14.opExtrude","CAP_FACE",FACE,{"disambiguationData":[OSD([sQuery(id+"F13.wireOp",EDGE,"E36.sketch_text.stroke-106"),sQuery(id+"F13.wireOp",EDGE,"E36.sketch_text.stroke-107"),sQuery(id+"F13.wireOp",EDGE,"E36.sketch_text.stroke-108"),sQuery(id+"F13.wireOp",EDGE,"E36.sketch_text.stroke-109"),sQuery(id+"F13.wireOp",EDGE,"E36.sketch_text.stroke-110"),sQuery(id+"F13.wireOp",EDGE,"E36.sketch_text.stroke-111"),sQuery(id+"F13.wireOp",EDGE,"E36.sketch_text.stroke-112"),sQuery(id+"F13.wireOp",EDGE,"E36.sketch_text.stroke-113"),sQuery(id+"F13.wireOp",EDGE,"E36.sketch_text.stroke-114"),sQuery(id+"F13.wireOp",EDGE,"E36.sketch_text.stroke-115"),sQuery(id+"F13.wireOp",EDGE,"E36.sketch_text.stroke-116"),sQuery(id+"F13.wireOp",EDGE,"E36.sketch_text.stroke-117"),sQuery(id+"F13.wireOp",EDGE,"E36.sketch_text.stroke-118"),sQuery(id+"F13.wireOp",EDGE,"E36.sketch_text.stroke-119"),sQuery(id+"F13.wireOp",EDGE,"E36.sketch_text.stroke-120"),sQuery(id+"F13.wireOp",EDGE,"E36.sketch_text.stroke-121"),sQuery(id+"F13.wireOp",EDGE,"E36.sketch_text.stroke-122")])],"isStart":false});
            var Q8;
            Q8=makeQuery(id+"F14.opExtrude","CAP_FACE",FACE,{"disambiguationData":[OSD([sQuery(id+"F13.wireOp",EDGE,"E36.sketch_text.stroke-123"),sQuery(id+"F13.wireOp",EDGE,"E36.sketch_text.stroke-124"),sQuery(id+"F13.wireOp",EDGE,"E36.sketch_text.stroke-125"),sQuery(id+"F13.wireOp",EDGE,"E36.sketch_text.stroke-126"),sQuery(id+"F13.wireOp",EDGE,"E36.sketch_text.stroke-127"),sQuery(id+"F13.wireOp",EDGE,"E36.sketch_text.stroke-128"),sQuery(id+"F13.wireOp",EDGE,"E36.sketch_text.stroke-129"),sQuery(id+"F13.wireOp",EDGE,"E36.sketch_text.stroke-130"),sQuery(id+"F13.wireOp",EDGE,"E36.sketch_text.stroke-131"),sQuery(id+"F13.wireOp",EDGE,"E36.sketch_text.stroke-132"),sQuery(id+"F13.wireOp",EDGE,"E36.sketch_text.stroke-133"),sQuery(id+"F13.wireOp",EDGE,"E36.sketch_text.stroke-134"),sQuery(id+"F13.wireOp",EDGE,"E36.sketch_text.stroke-135"),sQuery(id+"F13.wireOp",EDGE,"E36.sketch_text.stroke-136"),sQuery(id+"F13.wireOp",EDGE,"E36.sketch_text.stroke-137"),sQuery(id+"F13.wireOp",EDGE,"E36.sketch_text.stroke-138"),sQuery(id+"F13.wireOp",EDGE,"E36.sketch_text.stroke-139"),sQuery(id+"F13.wireOp",EDGE,"E36.sketch_text.stroke-140")])],"isStart":false});
            var Q9;
            Q9=makeQuery(id+"F14.opExtrude","CAP_FACE",FACE,{"disambiguationData":[OSD([sQuery(id+"F13.wireOp",EDGE,"E36.sketch_text.stroke-146"),sQuery(id+"F13.wireOp",EDGE,"E36.sketch_text.stroke-147"),sQuery(id+"F13.wireOp",EDGE,"E36.sketch_text.stroke-148"),sQuery(id+"F13.wireOp",EDGE,"E36.sketch_text.stroke-149")])],"isStart":false});
            var Q10;
            Q10=makeQuery(id+"F14.opExtrude","CAP_FACE",FACE,{"disambiguationData":[OSD([sQuery(id+"F13.wireOp",EDGE,"E36.sketch_text.stroke-141"),sQuery(id+"F13.wireOp",EDGE,"E36.sketch_text.stroke-142"),sQuery(id+"F13.wireOp",EDGE,"E36.sketch_text.stroke-143"),sQuery(id+"F13.wireOp",EDGE,"E36.sketch_text.stroke-144"),sQuery(id+"F13.wireOp",EDGE,"E36.sketch_text.stroke-145")])],"isStart":false});
            var Q11;
            Q11=makeQuery(id+"F14.opExtrude","CAP_FACE",FACE,{"disambiguationData":[OSD([sQuery(id+"F13.wireOp",EDGE,"E36.sketch_text.stroke-150"),sQuery(id+"F13.wireOp",EDGE,"E36.sketch_text.stroke-151"),sQuery(id+"F13.wireOp",EDGE,"E36.sketch_text.stroke-152"),sQuery(id+"F13.wireOp",EDGE,"E36.sketch_text.stroke-153"),sQuery(id+"F13.wireOp",EDGE,"E36.sketch_text.stroke-154"),sQuery(id+"F13.wireOp",EDGE,"E36.sketch_text.stroke-155"),sQuery(id+"F13.wireOp",EDGE,"E36.sketch_text.stroke-156"),sQuery(id+"F13.wireOp",EDGE,"E36.sketch_text.stroke-157"),sQuery(id+"F13.wireOp",EDGE,"E36.sketch_text.stroke-158"),sQuery(id+"F13.wireOp",EDGE,"E36.sketch_text.stroke-159"),sQuery(id+"F13.wireOp",EDGE,"E36.sketch_text.stroke-160"),sQuery(id+"F13.wireOp",EDGE,"E36.sketch_text.stroke-161"),sQuery(id+"F13.wireOp",EDGE,"E36.sketch_text.stroke-162"),sQuery(id+"F13.wireOp",EDGE,"E36.sketch_text.stroke-163"),sQuery(id+"F13.wireOp",EDGE,"E36.sketch_text.stroke-164"),sQuery(id+"F13.wireOp",EDGE,"E36.sketch_text.stroke-165"),sQuery(id+"F13.wireOp",EDGE,"E36.sketch_text.stroke-166")])],"isStart":false});
            var Q12;
            Q12=makeQuery(id+"F14.opExtrude","CAP_FACE",FACE,{"disambiguationData":[OSD([sQuery(id+"F13.wireOp",EDGE,"E36.sketch_text.stroke-167"),sQuery(id+"F13.wireOp",EDGE,"E36.sketch_text.stroke-168"),sQuery(id+"F13.wireOp",EDGE,"E36.sketch_text.stroke-169"),sQuery(id+"F13.wireOp",EDGE,"E36.sketch_text.stroke-170"),sQuery(id+"F13.wireOp",EDGE,"E36.sketch_text.stroke-171"),sQuery(id+"F13.wireOp",EDGE,"E36.sketch_text.stroke-172"),sQuery(id+"F13.wireOp",EDGE,"E36.sketch_text.stroke-173"),sQuery(id+"F13.wireOp",EDGE,"E36.sketch_text.stroke-174"),sQuery(id+"F13.wireOp",EDGE,"E36.sketch_text.stroke-175"),sQuery(id+"F13.wireOp",EDGE,"E36.sketch_text.stroke-176"),sQuery(id+"F13.wireOp",EDGE,"E36.sketch_text.stroke-177"),sQuery(id+"F13.wireOp",EDGE,"E36.sketch_text.stroke-178"),sQuery(id+"F13.wireOp",EDGE,"E36.sketch_text.stroke-179"),sQuery(id+"F13.wireOp",EDGE,"E36.sketch_text.stroke-180"),sQuery(id+"F13.wireOp",EDGE,"E36.sketch_text.stroke-181"),sQuery(id+"F13.wireOp",EDGE,"E36.sketch_text.stroke-182"),sQuery(id+"F13.wireOp",EDGE,"E36.sketch_text.stroke-183"),sQuery(id+"F13.wireOp",EDGE,"E36.sketch_text.stroke-184"),sQuery(id+"F13.wireOp",EDGE,"E36.sketch_text.stroke-185"),sQuery(id+"F13.wireOp",EDGE,"E36.sketch_text.stroke-186"),sQuery(id+"F13.wireOp",EDGE,"E36.sketch_text.stroke-187"),sQuery(id+"F13.wireOp",EDGE,"E36.sketch_text.stroke-188"),sQuery(id+"F13.wireOp",EDGE,"E36.sketch_text.stroke-189"),sQuery(id+"F13.wireOp",EDGE,"E36.sketch_text.stroke-190"),sQuery(id+"F13.wireOp",EDGE,"E36.sketch_text.stroke-191"),sQuery(id+"F13.wireOp",EDGE,"E36.sketch_text.stroke-192"),sQuery(id+"F13.wireOp",EDGE,"E36.sketch_text.stroke-193"),sQuery(id+"F13.wireOp",EDGE,"E36.sketch_text.stroke-194"),sQuery(id+"F13.wireOp",EDGE,"E36.sketch_text.stroke-195"),sQuery(id+"F13.wireOp",EDGE,"E36.sketch_text.stroke-196"),sQuery(id+"F13.wireOp",EDGE,"E36.sketch_text.stroke-197"),sQuery(id+"F13.wireOp",EDGE,"E36.sketch_text.stroke-198"),sQuery(id+"F13.wireOp",EDGE,"E36.sketch_text.stroke-199"),sQuery(id+"F13.wireOp",EDGE,"E36.sketch_text.stroke-200"),sQuery(id+"F13.wireOp",EDGE,"E36.sketch_text.stroke-201"),sQuery(id+"F13.wireOp",EDGE,"E36.sketch_text.stroke-202"),sQuery(id+"F13.wireOp",EDGE,"E36.sketch_text.stroke-203"),sQuery(id+"F13.wireOp",EDGE,"E36.sketch_text.stroke-204"),sQuery(id+"F13.wireOp",EDGE,"E36.sketch_text.stroke-205"),sQuery(id+"F13.wireOp",EDGE,"E36.sketch_text.stroke-206"),sQuery(id+"F13.wireOp",EDGE,"E36.sketch_text.stroke-207"),sQuery(id+"F13.wireOp",EDGE,"E36.sketch_text.stroke-208"),sQuery(id+"F13.wireOp",EDGE,"E36.sketch_text.stroke-209"),sQuery(id+"F13.wireOp",EDGE,"E36.sketch_text.stroke-210")])],"isStart":false});
            var Q13;
            Q13=makeQuery(id+"F14.opExtrude","CAP_FACE",FACE,{"disambiguationData":[OSD([sQuery(id+"F13.wireOp",EDGE,"E36.sketch_text.stroke-211"),sQuery(id+"F13.wireOp",EDGE,"E36.sketch_text.stroke-212"),sQuery(id+"F13.wireOp",EDGE,"E36.sketch_text.stroke-213"),sQuery(id+"F13.wireOp",EDGE,"E36.sketch_text.stroke-214")])],"isStart":false});
            var Q14;
            Q14=makeQuery(id+"F14.opExtrude","CAP_FACE",FACE,{"disambiguationData":[OSD([sQuery(id+"F13.wireOp",EDGE,"E36.sketch_text.stroke-215"),sQuery(id+"F13.wireOp",EDGE,"E36.sketch_text.stroke-216"),sQuery(id+"F13.wireOp",EDGE,"E36.sketch_text.stroke-217"),sQuery(id+"F13.wireOp",EDGE,"E36.sketch_text.stroke-218"),sQuery(id+"F13.wireOp",EDGE,"E36.sketch_text.stroke-219"),sQuery(id+"F13.wireOp",EDGE,"E36.sketch_text.stroke-220"),sQuery(id+"F13.wireOp",EDGE,"E36.sketch_text.stroke-221"),sQuery(id+"F13.wireOp",EDGE,"E36.sketch_text.stroke-222"),sQuery(id+"F13.wireOp",EDGE,"E36.sketch_text.stroke-223"),sQuery(id+"F13.wireOp",EDGE,"E36.sketch_text.stroke-224"),sQuery(id+"F13.wireOp",EDGE,"E36.sketch_text.stroke-225"),sQuery(id+"F13.wireOp",EDGE,"E36.sketch_text.stroke-226"),sQuery(id+"F13.wireOp",EDGE,"E36.sketch_text.stroke-227"),sQuery(id+"F13.wireOp",EDGE,"E36.sketch_text.stroke-228"),sQuery(id+"F13.wireOp",EDGE,"E36.sketch_text.stroke-229")])],"isStart":false});
            var Q15;
            Q15=makeQuery(id+"F14.opExtrude","CAP_FACE",FACE,{"disambiguationData":[OSD([sQuery(id+"F13.wireOp",EDGE,"E36.sketch_text.stroke-230"),sQuery(id+"F13.wireOp",EDGE,"E36.sketch_text.stroke-231"),sQuery(id+"F13.wireOp",EDGE,"E36.sketch_text.stroke-232"),sQuery(id+"F13.wireOp",EDGE,"E36.sketch_text.stroke-233"),sQuery(id+"F13.wireOp",EDGE,"E36.sketch_text.stroke-234"),sQuery(id+"F13.wireOp",EDGE,"E36.sketch_text.stroke-235"),sQuery(id+"F13.wireOp",EDGE,"E36.sketch_text.stroke-236"),sQuery(id+"F13.wireOp",EDGE,"E36.sketch_text.stroke-237")])],"isStart":false});
            var Q16;
            Q16=makeQuery(id+"F14.opExtrude","CAP_FACE",FACE,{"disambiguationData":[OSD([sQuery(id+"F13.wireOp",EDGE,"E36.sketch_text.stroke-238"),sQuery(id+"F13.wireOp",EDGE,"E36.sketch_text.stroke-239"),sQuery(id+"F13.wireOp",EDGE,"E36.sketch_text.stroke-240"),sQuery(id+"F13.wireOp",EDGE,"E36.sketch_text.stroke-241"),sQuery(id+"F13.wireOp",EDGE,"E36.sketch_text.stroke-242"),sQuery(id+"F13.wireOp",EDGE,"E36.sketch_text.stroke-243"),sQuery(id+"F13.wireOp",EDGE,"E36.sketch_text.stroke-244"),sQuery(id+"F13.wireOp",EDGE,"E36.sketch_text.stroke-245"),sQuery(id+"F13.wireOp",EDGE,"E36.sketch_text.stroke-246"),sQuery(id+"F13.wireOp",EDGE,"E36.sketch_text.stroke-247"),sQuery(id+"F13.wireOp",EDGE,"E36.sketch_text.stroke-248"),sQuery(id+"F13.wireOp",EDGE,"E36.sketch_text.stroke-249"),sQuery(id+"F13.wireOp",EDGE,"E36.sketch_text.stroke-250"),sQuery(id+"F13.wireOp",EDGE,"E36.sketch_text.stroke-251"),sQuery(id+"F13.wireOp",EDGE,"E36.sketch_text.stroke-252"),sQuery(id+"F13.wireOp",EDGE,"E36.sketch_text.stroke-253"),sQuery(id+"F13.wireOp",EDGE,"E36.sketch_text.stroke-254"),sQuery(id+"F13.wireOp",EDGE,"E36.sketch_text.stroke-255"),sQuery(id+"F13.wireOp",EDGE,"E36.sketch_text.stroke-256"),sQuery(id+"F13.wireOp",EDGE,"E36.sketch_text.stroke-257"),sQuery(id+"F13.wireOp",EDGE,"E36.sketch_text.stroke-258"),sQuery(id+"F13.wireOp",EDGE,"E36.sketch_text.stroke-259"),sQuery(id+"F13.wireOp",EDGE,"E36.sketch_text.stroke-260"),sQuery(id+"F13.wireOp",EDGE,"E36.sketch_text.stroke-261"),sQuery(id+"F13.wireOp",EDGE,"E36.sketch_text.stroke-262")])],"isStart":false});
            var Q17;
            Q17=makeQuery(id+"F14.opExtrude","CAP_FACE",FACE,{"disambiguationData":[OSD([sQuery(id+"F13.wireOp",EDGE,"E36.sketch_text.stroke-263"),sQuery(id+"F13.wireOp",EDGE,"E36.sketch_text.stroke-264"),sQuery(id+"F13.wireOp",EDGE,"E36.sketch_text.stroke-265"),sQuery(id+"F13.wireOp",EDGE,"E36.sketch_text.stroke-266"),sQuery(id+"F13.wireOp",EDGE,"E36.sketch_text.stroke-267"),sQuery(id+"F13.wireOp",EDGE,"E36.sketch_text.stroke-268"),sQuery(id+"F13.wireOp",EDGE,"E36.sketch_text.stroke-269"),sQuery(id+"F13.wireOp",EDGE,"E36.sketch_text.stroke-270")])],"isStart":false});
            fillet(context, id + "F15", {"entities" : qUnion([Q0, Q1, Q2, Q3, Q4, Q5, Q6, Q7, Q8, Q9, Q10, Q11, Q12, Q13, Q14, Q15, Q16, Q17]), "radius" : .1 * mm, "tangentPropagation" : true, "allowEdgeOverflow" : false});
        }
    });
